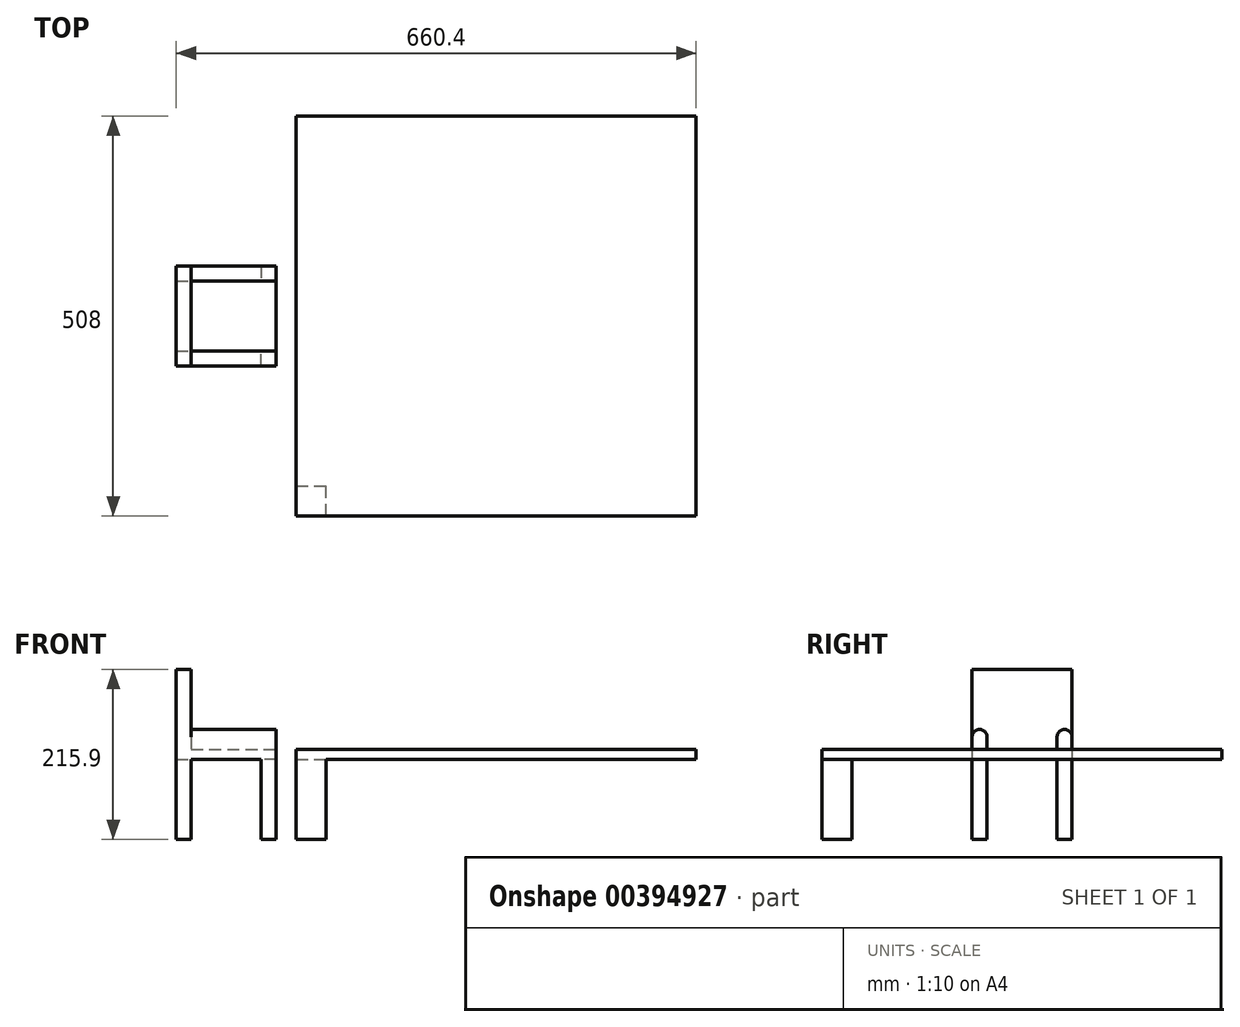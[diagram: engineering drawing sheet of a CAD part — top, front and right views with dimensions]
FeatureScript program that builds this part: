
annotation { "Feature Type Name" : "Feature", "Feature Type Description" : "" }
export const myFeature = defineFeature(function(context is Context, id is Id, definition is map)
    precondition{}
    {
        {
            var Q0;
            Q0=qCreatedBy(makeId("Top.planeOp"),FACE);
            var sketch = newSketch(context, id + "F0", { "sketchPlane" : qUnion([Q0])});
            skLineSegment(sketch, "E0.bottom", {"start": v(0, 0) * mm, "end": v(127, 0) * mm});
            skLineSegment(sketch, "E0.top", {"start": v(0, 127) * mm, "end": v(127, 127) * mm});
            skLineSegment(sketch, "E0.left", {"start": v(0, 0) * mm, "end": v(0, 127) * mm});
            skLineSegment(sketch, "E0.right", {"start": v(127, 0) * mm, "end": v(127, 127) * mm});
            skSolve(sketch);
        }
        {
            var Q0;
            Q0=makeQuery(id+"F0.imprint","IMPRINT",FACE,{"disambiguationData":[TD([[makeQuery(id+"F0.imprint","IMPRINT",EDGE,{"derivedFrom":sQuery(id+"F0.wireOp",EDGE,"E0.bottom")}),1.0]])]});
            extrude(context, id + "F1", {"entities" : qUnion([Q0]), "depth" : 12.7 * mm});
        }
        {
            var Q0;
            Q0=makeQuery(id+"F1.opExtrude","CAP_FACE",FACE,{"disambiguationData":[OSD([sQuery(id+"F0.wireOp",EDGE,"E0.bottom"),sQuery(id+"F0.wireOp",EDGE,"E0.top"),sQuery(id+"F0.wireOp",EDGE,"E0.left"),sQuery(id+"F0.wireOp",EDGE,"E0.right")])],"isStart":true});
            var sketch = newSketch(context, id + "F2", { "sketchPlane" : qUnion([Q0])});
            skLineSegment(sketch, "E1.bottom", {"start": v(0, -127) * mm, "end": v(19.05, -127) * mm});
            skLineSegment(sketch, "E1.top", {"start": v(0, -107.95) * mm, "end": v(19.05, -107.95) * mm});
            skLineSegment(sketch, "E1.left", {"start": v(0, -127) * mm, "end": v(0, -107.95) * mm});
            skLineSegment(sketch, "E1.right", {"start": v(19.05, -127) * mm, "end": v(19.05, -107.95) * mm});
            skLineSegment(sketch, "E2.bottom", {"start": v(0, 0) * mm, "end": v(19.05, 0) * mm});
            skLineSegment(sketch, "E2.top", {"start": v(0, -19.05) * mm, "end": v(19.05, -19.05) * mm});
            skLineSegment(sketch, "E2.left", {"start": v(0, 0) * mm, "end": v(0, -19.05) * mm});
            skLineSegment(sketch, "E2.right", {"start": v(19.05, 0) * mm, "end": v(19.05, -19.05) * mm});
            skLineSegment(sketch, "E3.bottom", {"start": v(127, 0) * mm, "end": v(107.95, 0) * mm});
            skLineSegment(sketch, "E3.top", {"start": v(127, -19.05) * mm, "end": v(107.95, -19.05) * mm});
            skLineSegment(sketch, "E3.left", {"start": v(127, 0) * mm, "end": v(127, -19.05) * mm});
            skLineSegment(sketch, "E3.right", {"start": v(107.95, 0) * mm, "end": v(107.95, -19.05) * mm});
            skLineSegment(sketch, "E4.bottom", {"start": v(127, -127) * mm, "end": v(107.95, -127) * mm});
            skLineSegment(sketch, "E4.top", {"start": v(127, -107.95) * mm, "end": v(107.95, -107.95) * mm});
            skLineSegment(sketch, "E4.left", {"start": v(127, -127) * mm, "end": v(127, -107.95) * mm});
            skLineSegment(sketch, "E4.right", {"start": v(107.95, -127) * mm, "end": v(107.95, -107.95) * mm});
            skSolve(sketch);
        }
        {
            var Q0;
            Q0=makeQuery(id+"F2.imprint","IMPRINT",FACE,{"disambiguationData":[TD([[makeQuery(id+"F2.imprint","IMPRINT",EDGE,{"derivedFrom":sQuery(id+"F2.wireOp",EDGE,"E2.bottom")}),-1.0]])]});
            var Q1;
            Q1=makeQuery(id+"F2.imprint","IMPRINT",FACE,{"disambiguationData":[TD([[makeQuery(id+"F2.imprint","IMPRINT",EDGE,{"derivedFrom":sQuery(id+"F2.wireOp",EDGE,"E1.bottom")}),1.0]])]});
            var Q2;
            Q2=makeQuery(id+"F2.imprint","IMPRINT",FACE,{"disambiguationData":[TD([[makeQuery(id+"F2.imprint","IMPRINT",EDGE,{"derivedFrom":sQuery(id+"F2.wireOp",EDGE,"E4.bottom")}),1.0]])]});
            var Q3;
            Q3=makeQuery(id+"F2.imprint","IMPRINT",FACE,{"disambiguationData":[TD([[makeQuery(id+"F2.imprint","IMPRINT",EDGE,{"derivedFrom":sQuery(id+"F2.wireOp",EDGE,"E3.bottom")}),-1.0]])]});
            extrude(context, id + "F3", {"entities" : qUnion([Q0, Q1, Q2, Q3]), "operationType" : NewBodyOperationType.ADD, "depth" : 101.6 * mm});
        }
        {
            var Q0;
            Q0=makeQuery(id+"F1.opExtrude","CAP_FACE",FACE,{"disambiguationData":[OSD([sQuery(id+"F0.wireOp",EDGE,"E0.bottom"),sQuery(id+"F0.wireOp",EDGE,"E0.top"),sQuery(id+"F0.wireOp",EDGE,"E0.left"),sQuery(id+"F0.wireOp",EDGE,"E0.right")])],"isStart":false});
            var sketch = newSketch(context, id + "F4", { "sketchPlane" : qUnion([Q0])});
            skLineSegment(sketch, "E5.bottom", {"start": v(0, 0) * mm, "end": v(19.05, 0) * mm});
            skLineSegment(sketch, "E5.top", {"start": v(0, 127) * mm, "end": v(19.05, 127) * mm});
            skLineSegment(sketch, "E5.left", {"start": v(0, 0) * mm, "end": v(0, 127) * mm});
            skLineSegment(sketch, "E5.right", {"start": v(19.05, 0) * mm, "end": v(19.05, 127) * mm});
            skSolve(sketch);
        }
        {
            var Q0;
            Q0=makeQuery(id+"F4.imprint","IMPRINT",FACE,{"disambiguationData":[TD([[makeQuery(id+"F4.imprint","IMPRINT",EDGE,{"derivedFrom":sQuery(id+"F4.wireOp",EDGE,"E5.bottom")}),1.0]])]});
            extrude(context, id + "F5", {"entities" : qUnion([Q0]), "operationType" : NewBodyOperationType.ADD, "depth" : 101.6 * mm});
        }
        {
            var Q0;
            Q0=makeQuery(id+"F1.opExtrude","CAP_FACE",FACE,{"disambiguationData":[OSD([sQuery(id+"F0.wireOp",EDGE,"E0.bottom"),sQuery(id+"F0.wireOp",EDGE,"E0.top"),sQuery(id+"F0.wireOp",EDGE,"E0.left"),sQuery(id+"F0.wireOp",EDGE,"E0.right")])],"isStart":false});
            var sketch = newSketch(context, id + "F6", { "sketchPlane" : qUnion([Q0])});
            skLineSegment(sketch, "E6.bottom", {"start": v(127, 0) * mm, "end": v(19.05, 0) * mm});
            skLineSegment(sketch, "E6.top", {"start": v(127, 19.05) * mm, "end": v(19.05, 19.05) * mm});
            skLineSegment(sketch, "E6.left", {"start": v(127, 0) * mm, "end": v(127, 19.05) * mm});
            skLineSegment(sketch, "E6.right", {"start": v(19.05, 0) * mm, "end": v(19.05, 19.05) * mm});
            skLineSegment(sketch, "E7.bottom", {"start": v(19.05, 107.95) * mm, "end": v(127, 107.95) * mm});
            skLineSegment(sketch, "E7.top", {"start": v(19.05, 127) * mm, "end": v(127, 127) * mm});
            skLineSegment(sketch, "E7.left", {"start": v(19.05, 107.95) * mm, "end": v(19.05, 127) * mm});
            skLineSegment(sketch, "E7.right", {"start": v(127, 107.95) * mm, "end": v(127, 127) * mm});
            skSolve(sketch);
        }
        {
            var Q0;
            Q0=makeQuery(id+"F6.imprint","IMPRINT",FACE,{"disambiguationData":[TD([[makeQuery(id+"F6.imprint","IMPRINT",EDGE,{"derivedFrom":sQuery(id+"F6.wireOp",EDGE,"E6.bottom")}),1.0]])]});
            var Q1;
            Q1=makeQuery(id+"F6.imprint","IMPRINT",FACE,{"disambiguationData":[TD([[makeQuery(id+"F6.imprint","IMPRINT",EDGE,{"derivedFrom":sQuery(id+"F6.wireOp",EDGE,"E7.bottom")}),1.0]])]});
            extrude(context, id + "F7", {"entities" : qUnion([Q0, Q1]), "operationType" : NewBodyOperationType.ADD, "depth" : 25.4 * mm});
        }
        {
            var Q0;
            Q0=makeQuery(id+"F7.opExtrude","CAP_EDGE",EDGE,{"disambiguationData":[OSD([sQuery(id+"F6.wireOp",EDGE,"E6.bottom")])],"isStart":false});
            var Q1;
            Q1=makeQuery(id+"F7.opExtrude","CAP_EDGE",EDGE,{"disambiguationData":[OSD([sQuery(id+"F6.wireOp",EDGE,"E6.top")])],"isStart":false});
            var Q2;
            Q2=makeQuery(id+"F7.opExtrude","CAP_EDGE",EDGE,{"disambiguationData":[OSD([sQuery(id+"F6.wireOp",EDGE,"E7.top")])],"isStart":false});
            var Q3;
            Q3=makeQuery(id+"F7.opExtrude","CAP_EDGE",EDGE,{"disambiguationData":[OSD([sQuery(id+"F6.wireOp",EDGE,"E7.bottom")])],"isStart":false});
            fillet(context, id + "F8", {"entities" : qUnion([Q0, Q1, Q2, Q3]), "radius" : 9.52 * mm, "tangentPropagation" : true, "allowEdgeOverflow" : false});
        }
        {
            var Q0;
            Q0=qCreatedBy(makeId("Top.planeOp"),FACE);
            var sketch = newSketch(context, id + "F9", { "sketchPlane" : qUnion([Q0])});
            skLineSegment(sketch, "E8.bottom", {"start": v(152.4, -190.5) * mm, "end": v(660.4, -190.5) * mm});
            skLineSegment(sketch, "E8.top", {"start": v(152.4, 317.5) * mm, "end": v(660.4, 317.5) * mm});
            skLineSegment(sketch, "E8.left", {"start": v(152.4, -190.5) * mm, "end": v(152.4, 317.5) * mm});
            skLineSegment(sketch, "E8.right", {"start": v(660.4, -190.5) * mm, "end": v(660.4, 317.5) * mm});
            skSolve(sketch);
        }
        {
            var Q0;
            Q0=makeQuery(id+"F9.imprint","IMPRINT",FACE,{"disambiguationData":[TD([[makeQuery(id+"F9.imprint","IMPRINT",EDGE,{"derivedFrom":sQuery(id+"F9.wireOp",EDGE,"E8.bottom")}),1.0]])]});
            extrude(context, id + "F10", {"entities" : qUnion([Q0]), "depth" : 12.7 * mm});
        }
        {
            var Q0;
            Q0=makeQuery(id+"F10.opExtrude","CAP_FACE",FACE,{"disambiguationData":[OSD([sQuery(id+"F9.wireOp",EDGE,"E8.bottom"),sQuery(id+"F9.wireOp",EDGE,"E8.top"),sQuery(id+"F9.wireOp",EDGE,"E8.left"),sQuery(id+"F9.wireOp",EDGE,"E8.right")])],"isStart":true});
            var sketch = newSketch(context, id + "F11", { "sketchPlane" : qUnion([Q0])});
            skLineSegment(sketch, "E9.bottom", {"start": v(152.4, 190.5) * mm, "end": v(190.5, 190.5) * mm});
            skLineSegment(sketch, "E9.top", {"start": v(152.4, 152.4) * mm, "end": v(190.5, 152.4) * mm});
            skLineSegment(sketch, "E9.left", {"start": v(152.4, 190.5) * mm, "end": v(152.4, 152.4) * mm});
            skLineSegment(sketch, "E9.right", {"start": v(190.5, 190.5) * mm, "end": v(190.5, 152.4) * mm});
            skSolve(sketch);
        }
        {
            var Q0;
            Q0=makeQuery(id+"F11.imprint","IMPRINT",FACE,{"disambiguationData":[TD([[makeQuery(id+"F11.imprint","IMPRINT",EDGE,{"derivedFrom":sQuery(id+"F11.wireOp",EDGE,"E9.bottom")}),-1.0]])]});
            var Q1;
            Q1=makeQuery(id+"F3.opExtrude","CAP_FACE",FACE,{"disambiguationData":[OSD([sQuery(id+"F2.wireOp",EDGE,"E3.bottom"),sQuery(id+"F2.wireOp",EDGE,"E3.top"),sQuery(id+"F2.wireOp",EDGE,"E3.left"),sQuery(id+"F2.wireOp",EDGE,"E3.right")])],"isStart":false});
            extrude(context, id + "F12", {"entities" : qUnion([Q0]), "operationType" : NewBodyOperationType.ADD, "endBound" : BoundingType.UP_TO_SURFACE, "endBoundEntityFace" : qUnion([Q1]), "depth" : 25.4 * mm});
        }
    });
